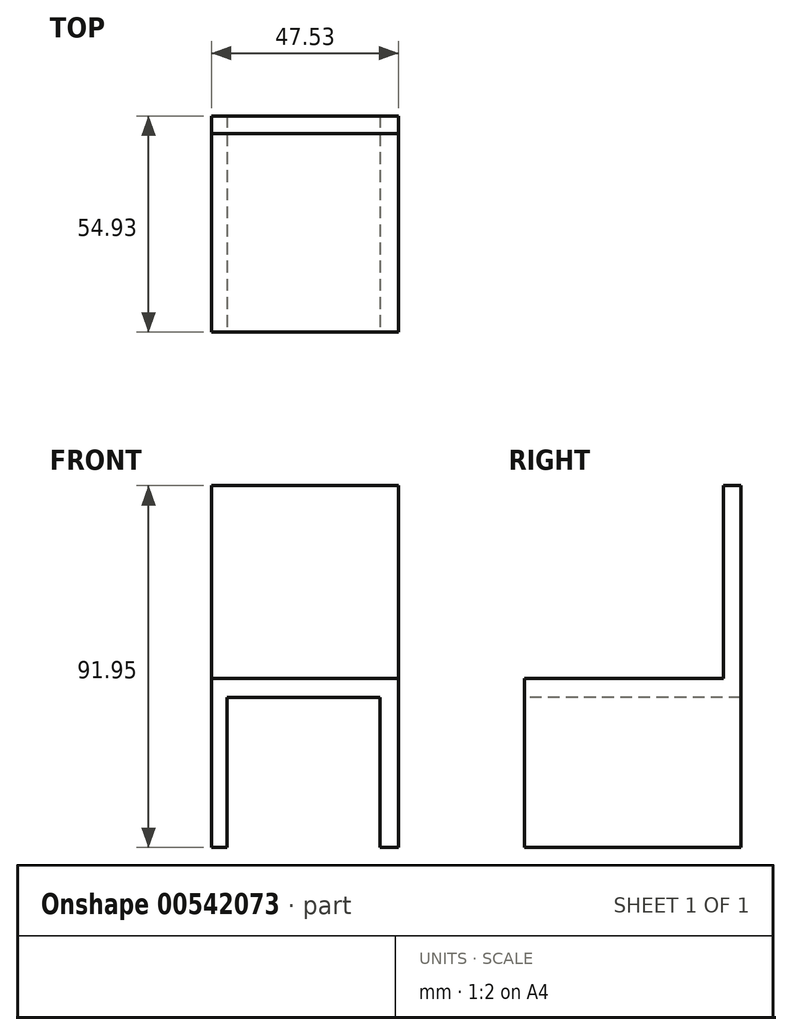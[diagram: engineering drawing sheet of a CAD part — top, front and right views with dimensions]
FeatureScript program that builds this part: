
annotation { "Feature Type Name" : "Feature", "Feature Type Description" : "" }
export const myFeature = defineFeature(function(context is Context, id is Id, definition is map)
    precondition{}
    {
        {
            var Q0;
            Q0=qCreatedBy(makeId("Top.planeOp"),FACE);
            var sketch = newSketch(context, id + "F0", { "sketchPlane" : qUnion([Q0])});
            skLineSegment(sketch, "E0.bottom", {"start": v(-136.62, 46.76) * mm, "end": v(-89.1, 46.76) * mm});
            skLineSegment(sketch, "E0.top", {"start": v(-136.62, -8.17) * mm, "end": v(-89.1, -8.17) * mm});
            skLineSegment(sketch, "E0.left", {"start": v(-136.62, 46.76) * mm, "end": v(-136.62, -8.17) * mm});
            skLineSegment(sketch, "E0.right", {"start": v(-89.1, 46.76) * mm, "end": v(-89.1, -8.17) * mm});
            skSolve(sketch);
        }
        {
            var Q0;
            Q0=makeQuery(id+"F0.imprint","IMPRINT",FACE,{"disambiguationData":[TD([[makeQuery(id+"F0.imprint","IMPRINT",EDGE,{"derivedFrom":sQuery(id+"F0.wireOp",EDGE,"E0.bottom")}),-1.0]])]});
            extrude(context, id + "F1", {"entities" : qUnion([Q0]), "depth" : 4.83 * mm, "offsetDistance" : 25.4 * mm});
        }
        {
            var Q0;
            Q0=makeQuery(id+"F1.opExtrude","CAP_FACE",FACE,{"disambiguationData":[OSD([sQuery(id+"F0.wireOp",EDGE,"E0.bottom"),sQuery(id+"F0.wireOp",EDGE,"E0.top"),sQuery(id+"F0.wireOp",EDGE,"E0.left"),sQuery(id+"F0.wireOp",EDGE,"E0.right")])],"isStart":false});
            var sketch = newSketch(context, id + "F2", { "sketchPlane" : qUnion([Q0])});
            skLineSegment(sketch, "E1.bottom", {"start": v(-136.62, 42.32) * mm, "end": v(-89.1, 42.32) * mm});
            skLineSegment(sketch, "E1.top", {"start": v(-136.62, 46.76) * mm, "end": v(-89.1, 46.76) * mm});
            skLineSegment(sketch, "E1.left", {"start": v(-136.62, 42.32) * mm, "end": v(-136.62, 46.76) * mm});
            skLineSegment(sketch, "E1.right", {"start": v(-89.1, 42.32) * mm, "end": v(-89.1, 46.76) * mm});
            skSolve(sketch);
        }
        {
            var Q0;
            Q0=makeQuery(id+"F2.imprint","IMPRINT",FACE,{"disambiguationData":[TD([[makeQuery(id+"F2.imprint","IMPRINT",EDGE,{"derivedFrom":sQuery(id+"F2.wireOp",EDGE,"E1.bottom")}),1.0]])]});
            extrude(context, id + "F3", {"entities" : qUnion([Q0]), "operationType" : NewBodyOperationType.ADD, "depth" : 49.02 * mm, "offsetDistance" : 25.4 * mm});
        }
        {
            var Q0;
            Q0=makeQuery(id+"F1.opExtrude","CAP_FACE",FACE,{"disambiguationData":[OSD([sQuery(id+"F0.wireOp",EDGE,"E0.bottom"),sQuery(id+"F0.wireOp",EDGE,"E0.top"),sQuery(id+"F0.wireOp",EDGE,"E0.left"),sQuery(id+"F0.wireOp",EDGE,"E0.right")])],"isStart":true});
            var sketch = newSketch(context, id + "F4", { "sketchPlane" : qUnion([Q0])});
            skLineSegment(sketch, "E2.bottom", {"start": v(-93.84, -46.76) * mm, "end": v(-89.1, -46.76) * mm});
            skLineSegment(sketch, "E2.top", {"start": v(-93.84, 8.17) * mm, "end": v(-89.1, 8.17) * mm});
            skLineSegment(sketch, "E2.left", {"start": v(-93.84, -46.76) * mm, "end": v(-93.84, 8.17) * mm});
            skLineSegment(sketch, "E2.right", {"start": v(-89.1, -46.76) * mm, "end": v(-89.1, 8.17) * mm});
            skSolve(sketch);
        }
        {
            var Q0;
            Q0=makeQuery(id+"F4.imprint","IMPRINT",FACE,{"disambiguationData":[TD([[makeQuery(id+"F4.imprint","IMPRINT",EDGE,{"derivedFrom":sQuery(id+"F4.wireOp",EDGE,"E2.bottom")}),1.0]])]});
            extrude(context, id + "F5", {"entities" : qUnion([Q0]), "operationType" : NewBodyOperationType.ADD, "depth" : 38.1 * mm, "offsetDistance" : 25.4 * mm});
        }
        {
            var Q0;
            Q0=makeQuery(id+"F1.opExtrude","CAP_FACE",FACE,{"disambiguationData":[OSD([sQuery(id+"F0.wireOp",EDGE,"E0.bottom"),sQuery(id+"F0.wireOp",EDGE,"E0.top"),sQuery(id+"F0.wireOp",EDGE,"E0.left"),sQuery(id+"F0.wireOp",EDGE,"E0.right")])],"isStart":true});
            var sketch = newSketch(context, id + "F6", { "sketchPlane" : qUnion([Q0])});
            skLineSegment(sketch, "E3.bottom", {"start": v(-132.65, -46.76) * mm, "end": v(-136.62, -46.76) * mm});
            skLineSegment(sketch, "E3.top", {"start": v(-132.65, 8.17) * mm, "end": v(-136.62, 8.17) * mm});
            skLineSegment(sketch, "E3.left", {"start": v(-132.65, -46.76) * mm, "end": v(-132.65, 8.17) * mm});
            skLineSegment(sketch, "E3.right", {"start": v(-136.62, -46.76) * mm, "end": v(-136.62, 8.17) * mm});
            skSolve(sketch);
        }
        {
            var Q0;
            Q0=makeQuery(id+"F6.imprint","IMPRINT",FACE,{"disambiguationData":[TD([[makeQuery(id+"F6.imprint","IMPRINT",EDGE,{"derivedFrom":sQuery(id+"F6.wireOp",EDGE,"E3.bottom")}),1.0]])]});
            extrude(context, id + "F7", {"entities" : qUnion([Q0]), "operationType" : NewBodyOperationType.ADD, "depth" : 38.1 * mm, "offsetDistance" : 25.4 * mm});
        }
    });
